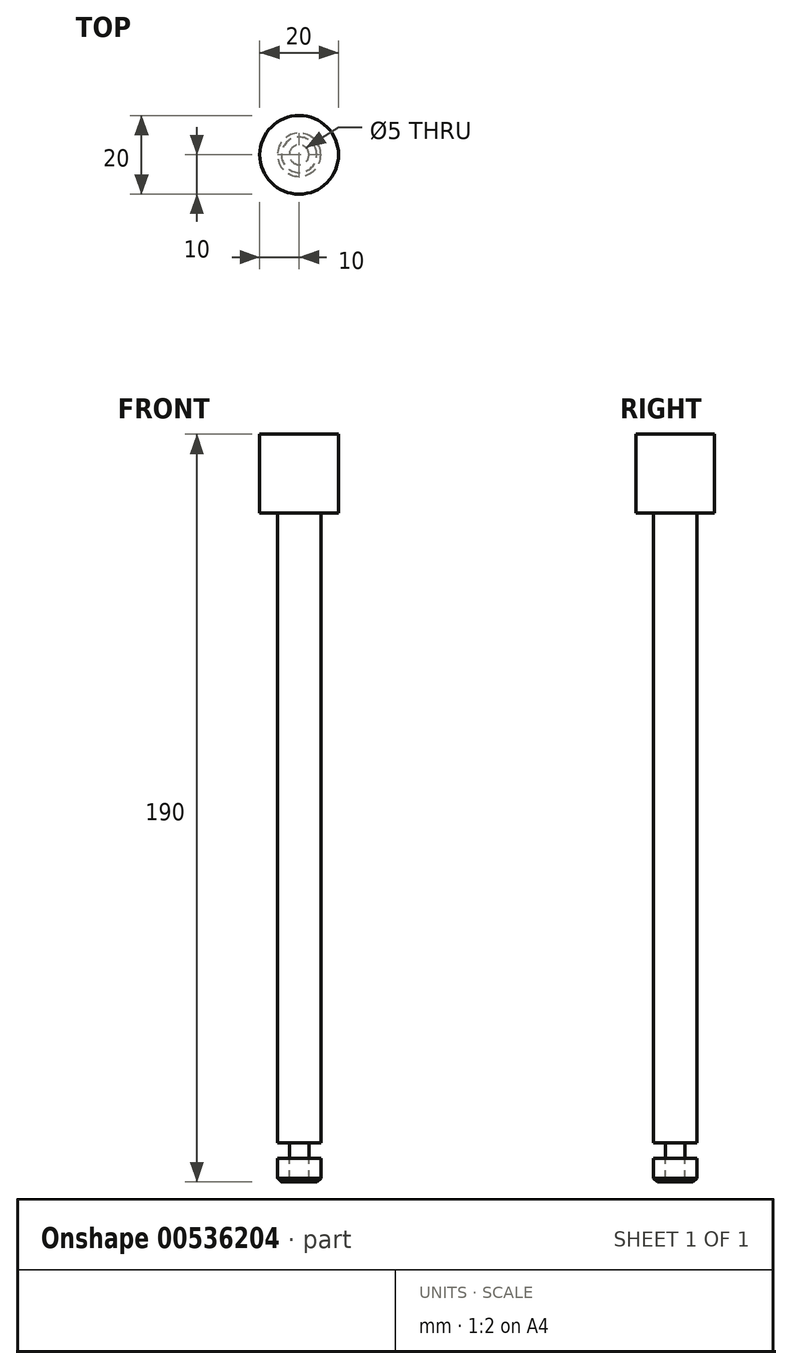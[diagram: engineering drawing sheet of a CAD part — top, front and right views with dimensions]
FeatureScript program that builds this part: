
annotation { "Feature Type Name" : "Feature", "Feature Type Description" : "" }
export const myFeature = defineFeature(function(context is Context, id is Id, definition is map)
    precondition{}
    {
        {
            var Q0;
            Q0=qCreatedBy(makeId("Top.planeOp"),FACE);
            var sketch = newSketch(context, id + "F0", { "sketchPlane" : qUnion([Q0])});
            skCircle(sketch, "E0", {"center": v(0, 0) * mm, "radius": 10 * mm});
            skSolve(sketch);
        }
        {
            var Q0;
            Q0=makeQuery(id+"F0.imprint","IMPRINT",FACE,{"disambiguationData":[TD([[makeQuery(id+"F0.imprint","IMPRINT",EDGE,{"derivedFrom":sQuery(id+"F0.wireOp",EDGE,"E0")}),1.0]])]});
            extrude(context, id + "F1", {"entities" : qUnion([Q0]), "depth" : 20 * mm, "offsetDistance" : 25 * mm});
        }
        {
            var Q0;
            Q0=makeQuery(id+"F1.opExtrude","CAP_FACE",FACE,{"disambiguationData":[OSD([sQuery(id+"F0.wireOp",EDGE,"E0")])],"isStart":true});
            var sketch = newSketch(context, id + "F2", { "sketchPlane" : qUnion([Q0])});
            skCircle(sketch, "E1", {"center": v(0, 0) * mm, "radius": 5.5 * mm});
            skSolve(sketch);
        }
        {
            var Q0;
            Q0=makeQuery(id+"F2.imprint","IMPRINT",FACE,{"disambiguationData":[TD([[makeQuery(id+"F2.imprint","IMPRINT",EDGE,{"derivedFrom":sQuery(id+"F2.wireOp",EDGE,"E1")}),1.0]])]});
            extrude(context, id + "F3", {"entities" : qUnion([Q0]), "operationType" : NewBodyOperationType.ADD, "depth" : 160 * mm, "offsetDistance" : 25 * mm});
        }
        {
            var Q0;
            Q0=makeQuery(id+"F3.opExtrude","CAP_FACE",FACE,{"disambiguationData":[OSD([sQuery(id+"F2.wireOp",EDGE,"E1")])],"isStart":false});
            var sketch = newSketch(context, id + "F4", { "sketchPlane" : qUnion([Q0])});
            skCircle(sketch, "E2", {"center": v(0, 0) * mm, "radius": 2.5 * mm});
            skSolve(sketch);
        }
        {
            var Q0;
            Q0=makeQuery(id+"F4.imprint","IMPRINT",FACE,{"disambiguationData":[TD([[makeQuery(id+"F4.imprint","IMPRINT",EDGE,{"derivedFrom":sQuery(id+"F4.wireOp",EDGE,"E2")}),1.0]])]});
            extrude(context, id + "F5", {"entities" : qUnion([Q0]), "operationType" : NewBodyOperationType.ADD, "depth" : 4 * mm, "offsetDistance" : 25 * mm});
        }
        {
            var Q0;
            Q0=makeQuery(id+"F5.opExtrude","CAP_FACE",FACE,{"disambiguationData":[OSD([sQuery(id+"F4.wireOp",EDGE,"E2")])],"isStart":false});
            var sketch = newSketch(context, id + "F6", { "sketchPlane" : qUnion([Q0])});
            skCircle(sketch, "E3", {"center": v(0, 0) * mm, "radius": 5.5 * mm});
            skSolve(sketch);
        }
        {
            var Q0;
            Q0=makeQuery(id+"F6.imprint","IMPRINT",FACE,{"disambiguationData":[TD([[makeQuery(id+"F6.imprint","IMPRINT",EDGE,{"derivedFrom":sQuery(id+"F6.wireOp",EDGE,"E3")}),1.0]])]});
            extrude(context, id + "F7", {"entities" : qUnion([Q0]), "depth" : 6 * mm, "offsetDistance" : 25 * mm});
        }
        {
            var Q0;
            Q0=makeQuery(id+"F7.opExtrude","CAP_EDGE",EDGE,{"disambiguationData":[OSD([sQuery(id+"F6.wireOp",EDGE,"E3")])],"isStart":false});
            chamfer(context, id + "F8", {"entities" : qUnion([Q0]), "width" : 1 * mm, "tangentPropagation" : true});
        }
    });
